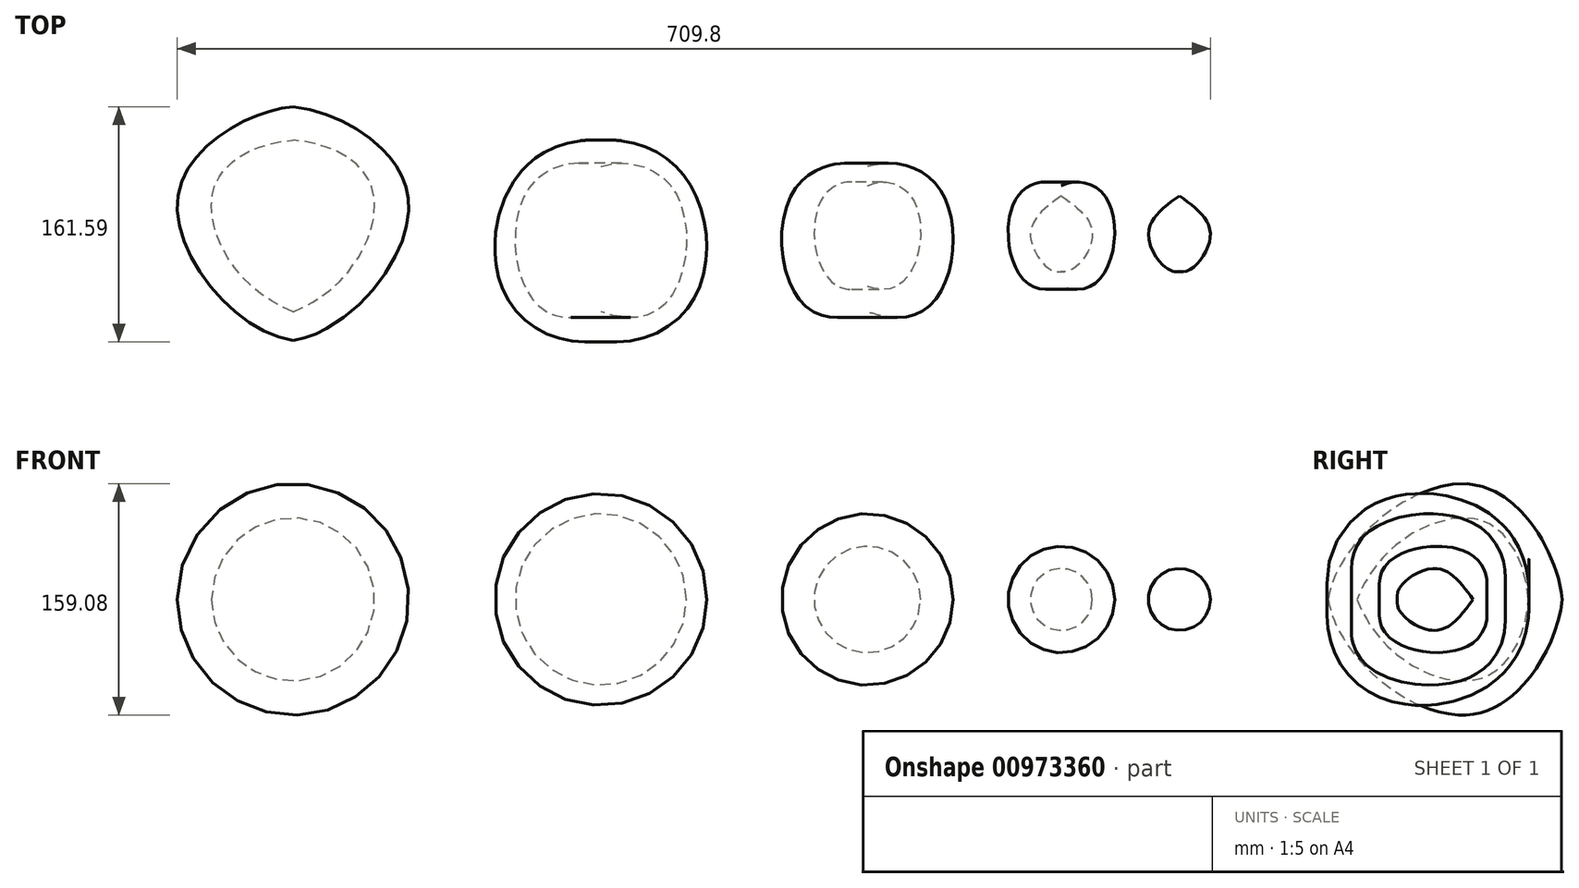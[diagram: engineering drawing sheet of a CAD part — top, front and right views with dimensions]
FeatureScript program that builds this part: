
annotation { "Feature Type Name" : "Feature", "Feature Type Description" : "" }
export const myFeature = defineFeature(function(context is Context, id is Id, definition is map)
    precondition{}
    {
        {
            var Q0;
            Q0=qCreatedBy(makeId("Top.planeOp"),FACE);
            var sketch = newSketch(context, id + "F0", { "sketchPlane" : qUnion([Q0])});
            skFitSpline(sketch, "E0", {"points": [v(0, 0) * mm, v(21.24, -28.18) * mm, v(0, -51.86) * mm, v(-7.35, 0) * mm, v(29.81, 0) * mm, v(19.2, -62.69) * mm, v(-35.73, -25.73) * mm, v(0, 20.21) * mm, v(52.48, 0) * mm, v(40.23, -77.8) * mm, v(-32.06, -58.8) * mm, v(-51.46, 11.84) * mm, v(14.5, 37.78) * mm, v(65.34, 0) * mm, v(61.46, -74.94) * mm, v(-13.07, -95.97) * mm, v(-79.02, 0) * mm, v(-13.48, 58.8) * mm, v(34.5, 57.58) * mm], "startDerivative": vector(801.31, -582.61) * mm, "endDerivative": vector(891.28, -191.96) * mm});
            skLineSegment(sketch, "E1", {"start": v(14.5, 37.78) * mm, "end": v(34.5, 57.58) * mm});
            skLineSegment(sketch, "E2", {"start": v(0, 76.56) * mm, "end": v(0, -117.4) * mm});
            skSolve(sketch);
        }
        {
            var Q0;
            {var subQ0=sQuery(id+"F0.wireOp",EDGE,"E2");var subQ1=sQuery(id+"F0.wireOp",EDGE,"E0");var subQ2=makeQuery(id+"F0.imprint","INTERSECT",VERTEX,{"disambiguationData":[OD(0.0)],"derivedFrom":[subQ1,subQ0]});Q0=makeQuery(id+"F0.imprint","IMPRINT",FACE,{"disambiguationData":[TD([[makeQuery(id+"F0.imprint","IMPRINT",EDGE,{"disambiguationData":[TD([[subQ2,-1.0]])],"derivedFrom":subQ1}),-1.0]])]});}
            var Q1;
            Q1=sQuery(id+"F0.wireOp",EDGE,"E2");
            revolve(context, id + "F1", {"surfaceOperationType" : NewSurfaceOperationType.NEW, "entities" : qUnion([Q0]), "axis" : qUnion([Q1]), "revolveType" : RevolveType.FULL});
        }
        {
            var Q0;
            {var subQ0=sQuery(id+"F0.wireOp",EDGE,"E2");var subQ1=sQuery(id+"F0.wireOp",EDGE,"E0");var subQ2=makeQuery(id+"F0.imprint","INTERSECT",VERTEX,{"disambiguationData":[OD(0.0)],"derivedFrom":[subQ1,subQ0]});Q0=makeQuery(id+"F0.imprint","IMPRINT",FACE,{"disambiguationData":[TD([[makeQuery(id+"F0.imprint","IMPRINT",EDGE,{"disambiguationData":[TD([[subQ2,-1.0]])],"derivedFrom":subQ1}),1.0]])]});}
            var Q1;
            Q1=sQuery(id+"F0.wireOp",EDGE,"E2");
            revolve(context, id + "F2", {"surfaceOperationType" : NewSurfaceOperationType.NEW, "entities" : qUnion([Q0]), "axis" : qUnion([Q1]), "revolveType" : RevolveType.FULL});
        }
        {
            var Q0;
            {var subQ0=sQuery(id+"F0.wireOp",EDGE,"E2");var subQ1=sQuery(id+"F0.wireOp",EDGE,"E0");var subQ2=makeQuery(id+"F0.imprint","INTERSECT",VERTEX,{"disambiguationData":[OD(4.0)],"derivedFrom":[subQ1,subQ0]});Q0=makeQuery(id+"F0.imprint","IMPRINT",FACE,{"disambiguationData":[TD([[makeQuery(id+"F0.imprint","IMPRINT",EDGE,{"disambiguationData":[TD([[subQ2,-1.0]])],"derivedFrom":subQ1}),1.0]])]});}
            var Q1;
            Q1=sQuery(id+"F0.wireOp",EDGE,"E2");
            revolve(context, id + "F3", {"surfaceOperationType" : NewSurfaceOperationType.NEW, "entities" : qUnion([Q0]), "axis" : qUnion([Q1]), "revolveType" : RevolveType.FULL});
        }
        {
            var Q0;
            {var subQ0=sQuery(id+"F0.wireOp",EDGE,"E2");var subQ1=sQuery(id+"F0.wireOp",EDGE,"E0");var subQ6=makeQuery(id+"F0.imprint","INTERSECT",VERTEX,{"disambiguationData":[OD(6.0)],"derivedFrom":[subQ1,subQ0]});Q0=makeQuery(id+"F0.imprint","IMPRINT",FACE,{"disambiguationData":[TD([[makeQuery(id+"F0.imprint","IMPRINT",EDGE,{"disambiguationData":[TD([[subQ6,-1.0]])],"derivedFrom":subQ1}),1.0]])]});}
            var Q1;
            Q1=sQuery(id+"F0.wireOp",EDGE,"E2");
            revolve(context, id + "F4", {"surfaceOperationType" : NewSurfaceOperationType.NEW, "entities" : qUnion([Q0]), "axis" : qUnion([Q1]), "revolveType" : RevolveType.FULL});
        }
        {
            var Q0;
            {var subQ0=sQuery(id+"F0.wireOp",EDGE,"E2");var subQ1=sQuery(id+"F0.wireOp",EDGE,"E0");var subQ2=makeQuery(id+"F0.imprint","INTERSECT",VERTEX,{"disambiguationData":[OD(7.0)],"derivedFrom":[subQ1,subQ0]});Q0=makeQuery(id+"F0.imprint","IMPRINT",FACE,{"disambiguationData":[TD([[makeQuery(id+"F0.imprint","IMPRINT",EDGE,{"disambiguationData":[TD([[subQ2,-1.0]])],"derivedFrom":subQ1}),1.0]])]});}
            var Q1;
            Q1=sQuery(id+"F0.wireOp",EDGE,"E2");
            revolve(context, id + "F5", {"surfaceOperationType" : NewSurfaceOperationType.NEW, "entities" : qUnion([Q0]), "axis" : qUnion([Q1]), "revolveType" : RevolveType.FULL});
        }
        {
            var Q0;
            Q0=makeQuery(id+"F1.opRevolve","SWEPT_BODY",BODY,{"disambiguationData":[OSD([sQuery(id+"F0.wireOp",EDGE,"E0"),sQuery(id+"F0.wireOp",EDGE,"E2")])]});
            transform(context, id + "F6", {"entities" : qUnion([Q0]), "transformType" : TransformType.TRANSLATION_3D, "dx" : -160.92 * mm, "dy" : 0 * mm, "dz" : 0 * mm, "makeCopy" : false});
        }
        {
            var Q0;
            Q0=makeQuery(id+"F2.opRevolve","SWEPT_BODY",BODY,{"disambiguationData":[OSD([sQuery(id+"F0.wireOp",EDGE,"E0"),sQuery(id+"F0.wireOp",EDGE,"E2")])]});
            transform(context, id + "F7", {"entities" : qUnion([Q0]), "transformType" : TransformType.TRANSLATION_3D, "dx" : -242 * mm, "dy" : 0 * mm, "dz" : 0 * mm, "makeCopy" : false});
        }
        {
            var Q0;
            Q0=makeQuery(id+"F3.opRevolve","SWEPT_BODY",BODY,{"disambiguationData":[OSD([sQuery(id+"F0.wireOp",EDGE,"E0"),sQuery(id+"F0.wireOp",EDGE,"E2")])]});
            transform(context, id + "F8", {"entities" : qUnion([Q0]), "transformType" : TransformType.TRANSLATION_3D, "dx" : -375.32 * mm, "dy" : 0 * mm, "dz" : 0 * mm, "makeCopy" : false});
        }
        {
            var Q0;
            Q0=makeQuery(id+"F4.opRevolve","SWEPT_BODY",BODY,{"disambiguationData":[OSD([sQuery(id+"F0.wireOp",EDGE,"E0"),sQuery(id+"F0.wireOp",EDGE,"E2")])]});
            transform(context, id + "F9", {"entities" : qUnion([Q0]), "transformType" : TransformType.TRANSLATION_3D, "dx" : -558.44 * mm, "dy" : 0 * mm, "dz" : 0 * mm, "makeCopy" : false});
        }
        {
            var Q0;
            Q0=makeQuery(id+"F5.opRevolve","SWEPT_BODY",BODY,{"disambiguationData":[OSD([sQuery(id+"F0.wireOp",EDGE,"E0"),sQuery(id+"F0.wireOp",EDGE,"E2")])]});
            transform(context, id + "F10", {"entities" : qUnion([Q0]), "transformType" : TransformType.TRANSLATION_3D, "dx" : -769.9 * mm, "dy" : 0 * mm, "dz" : 0 * mm, "makeCopy" : false});
        }
    });
